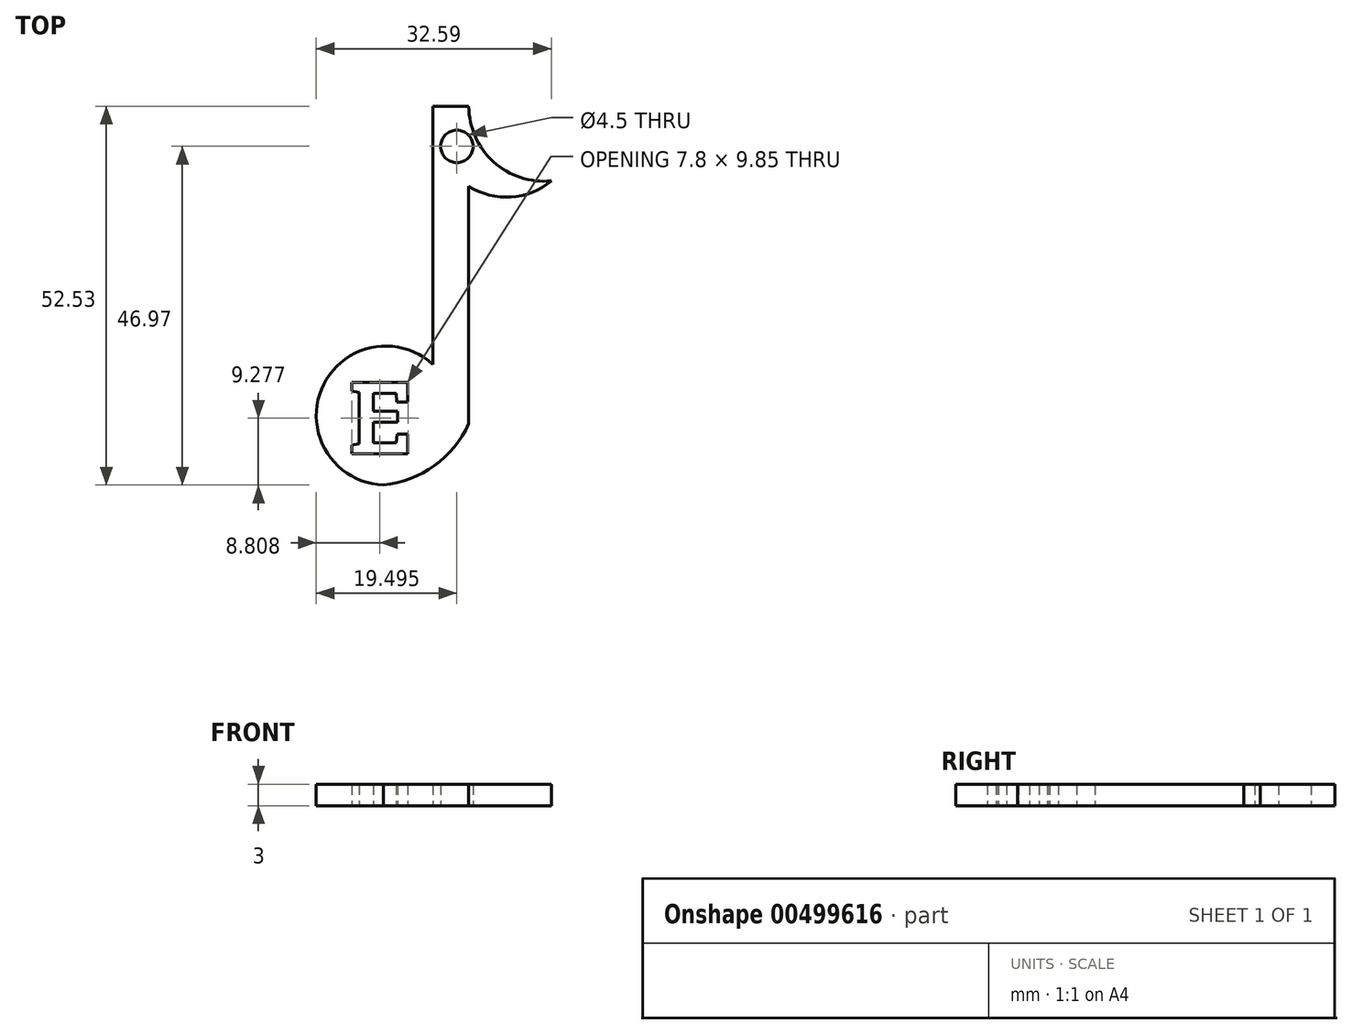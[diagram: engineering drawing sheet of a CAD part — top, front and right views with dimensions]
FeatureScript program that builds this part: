
annotation { "Feature Type Name" : "Feature", "Feature Type Description" : "" }
export const myFeature = defineFeature(function(context is Context, id is Id, definition is map)
    precondition{}
    {
        {
            var Q0;
            Q0=qCreatedBy(makeId("Top.planeOp"),FACE);
            var sketch = newSketch(context, id + "F0", { "sketchPlane" : qUnion([Q0])});
            skLineSegment(sketch, "E0", {"start": v(2.07, -20.72) * mm, "end": v(1.07, -20.72) * mm});
            skLineSegment(sketch, "E1", {"start": v(2.07, 29.28) * mm, "end": v(7.07, 29.28) * mm});
            skPoint(sketch, "E2.startSnap0", {"position": v(7.07, 4.28) * mm});
            skArc(sketch, "E3", {"start": v(2.07, -6.51) * mm, "mid": v(-14.08, -13.62) * mm, "end": v(2.07, -20.72) * mm});
            skLineSegment(sketch, "E4", {"start": v(2.07, 29.28) * mm, "end": v(2.07, 22.33) * mm});
            skPoint(sketch, "E5.visualSharp", {"position": v(7.07, -20.72) * mm});
            skArc(sketch, "E6", {"start": v(-4.77, -23.25) * mm, "mid": v(2.3, -20.57) * mm, "end": v(7.07, -14.72) * mm});
            skLineSegment(sketch, "E7", {"start": v(2.07, -6.51) * mm, "end": v(2.07, 22.33) * mm});
            skLineSegment(sketch, "E8", {"start": v(7.07, -14.72) * mm, "end": v(7.07, 18.18) * mm});
            skArc(sketch, "E9", {"start": v(7.07, 29.28) * mm, "mid": v(10.5, 21.57) * mm, "end": v(18.51, 18.94) * mm});
            skArc(sketch, "E10", {"start": v(7.07, 18.18) * mm, "mid": v(12.92, 16.7) * mm, "end": v(18.51, 18.94) * mm});
            skCircle(sketch, "E11", {"center": v(5.42, 23.72) * mm, "radius": 2.25 * mm});
            skText(sketch, "E12", { "text": "E", "fontName": "RobotoSlab-Bold.ttf"});
            const initialGuessF0  = {"E12": [-0.00955, -0.0189, 1, 0, 0.00998]};
            skSetInitialGuess(sketch, initialGuessF0);
            skSolve(sketch);
        }
        {
            var Q0;
            Q0=makeQuery(id+"F0.imprint","IMPRINT",FACE,{"disambiguationData":[TD([[makeQuery(id+"F0.imprint","IMPRINT",EDGE,{"derivedFrom":sQuery(id+"F0.wireOp",EDGE,"E1")}),-1.0]])]});
            extrude(context, id + "F1", {"entities" : qUnion([Q0]), "depth" : 3 * mm});
        }
    });
